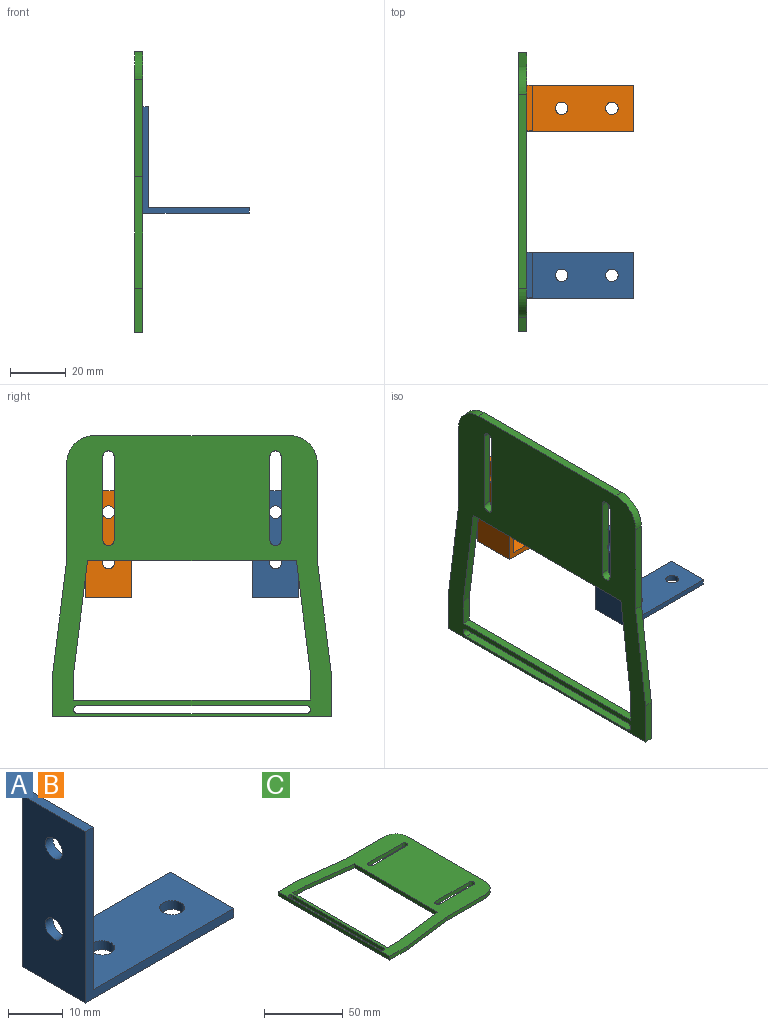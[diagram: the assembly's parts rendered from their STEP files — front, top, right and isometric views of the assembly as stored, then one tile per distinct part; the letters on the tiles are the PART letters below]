
ASSEMBLY  parts=3 mates=2
PART A: 12 faces, bbox 38.3x16.3x38.3 mm
  f0: plane 36.3x16.3mm, normal (0,0,1), area 559.9mm2, adj f1,f3,f4,f5,f6,f11
  f1: plane 38.3x38.3mm, normal (0,1,0), area 149.2mm2, adj f0,f2,f6,f7,f8,f11
  f2: plane 38.3x16.3mm, normal (-1,0,0), area 592.5mm2, adj f1,f3,f7,f8,f9,f10
  f3: plane 38.3x38.3mm, normal (0,-1,0), area 149.2mm2, adj f0,f2,f6,f7,f8,f11
  f4: cylinder r=2.25mm len=4.5mm, axis (0,0,-1), area 28.3mm2, adj f0,f7
  f5: cylinder r=2.25mm len=4.5mm, axis (0,0,-1), area 28.3mm2, adj f0,f7
  f6: plane 16.3x2mm, normal (1,0,0), area 32.6mm2, adj f0,f1,f3,f7
  f7: plane 38.3x16.3mm, normal (0,0,-1), area 592.5mm2, adj f1,f2,f3,f4,f5,f6
  f8: plane 16.3x2mm, normal (0,0,1), area 32.6mm2, adj f1,f2,f3,f11
  f9: cylinder r=2.25mm len=4.5mm, axis (-1,0,0), area 28.3mm2, adj f2,f11
  f10: cylinder r=2.25mm len=4.5mm, axis (-1,0,0), area 28.3mm2, adj f2,f11
  f11: plane 36.3x16.3mm, normal (1,0,0), area 559.9mm2, adj f0,f1,f3,f8,f9,f10
PART B: same geometry as A
PART C: 30 faces, bbox 100.9x100x3 mm
  f0: cylinder r=2mm len=4mm, axis (0,0,-1), area 18.8mm2, adj f1,f27,f28,f29
  f1: plane 30x3mm, normal (0,-1,0), area 90mm2, adj f0,f2,f28,f29
  f2: cylinder r=2mm len=4mm, axis (0,0,-1), area 18.8mm2, adj f1,f27,f28,f29
  f3: plane 85x3mm, normal (1,0,0), area 255mm2, adj f4,f23,f28,f29
  f4: plane 10x3mm, normal (0,-1,0), area 30mm2, adj f3,f5,f28,f29
  f5: plane 40x5mm, normal (-0.12,-0.99,0), area 120.9mm2, adj f4,f6,f28,f29
  f6: plane 75x3mm, normal (-1,0,0), area 225mm2, adj f5,f7,f28,f29
  f7: plane 40x5mm, normal (-0.12,0.99,0), area 120.9mm2, adj f6,f23,f28,f29
  f8: cylinder r=10mm len=10mm, axis (0,0,-1), area 47.1mm2, adj f9,f24,f28,f29
  f9: plane 35x3mm, normal (0,1,0), area 105mm2, adj f8,f10,f28,f29
  f10: plane 40x5mm, normal (0.12,0.99,0), area 120.9mm2, adj f9,f11,f28,f29
  f11: plane 15.9x3mm, normal (0,1,0), area 47.7mm2, adj f10,f12,f28,f29
  f12: plane 100x3mm, normal (-1,0,0), area 300mm2, adj f11,f13,f28,f29
  f13: plane 15.9x3mm, normal (0,-1,0), area 47.7mm2, adj f12,f14,f28,f29
  f14: plane 40x5mm, normal (0.12,-0.99,0), area 120.9mm2, adj f13,f15,f28,f29
  f15: plane 35x3mm, normal (0,-1,0), area 105mm2, adj f14,f16,f28,f29
  f16: cylinder r=10mm len=10mm, axis (0,0,-1), area 47.1mm2, adj f15,f24,f28,f29
  f17: cylinder r=1.5mm len=3mm, axis (0,0,-1), area 14.1mm2, adj f18,f25,f28,f29
  f18: plane 82x3mm, normal (-1,0,0), area 246mm2, adj f17,f19,f28,f29
  f19: cylinder r=1.5mm len=3mm, axis (0,0,-1), area 14.1mm2, adj f18,f25,f28,f29
  f20: plane 30x3mm, normal (0,1,0), area 90mm2, adj f21,f26,f28,f29
  f21: cylinder r=2mm len=4mm, axis (0,0,-1), area 18.8mm2, adj f20,f22,f28,f29
  f22: plane 30x3mm, normal (0,-1,0), area 90mm2, adj f21,f26,f28,f29
  f23: plane 10x3mm, normal (0,1,0), area 30mm2, adj f3,f7,f28,f29
  f24: plane 70x3mm, normal (1,0,0), area 210mm2, adj f8,f16,f28,f29
  f25: plane 82x3mm, normal (1,0,0), area 246mm2, adj f17,f19,f28,f29
  f26: cylinder r=2mm len=4mm, axis (0,0,-1), area 18.8mm2, adj f20,f22,f28,f29
  f27: plane 30x3mm, normal (0,1,0), area 90mm2, adj f0,f2,f28,f29
  f28: plane 100.9x100mm, normal (0,0,1), area 4828.9mm2, adj f0,f1,f2,f3,f4,f5,f6,f7
  f29: plane 100.9x100mm, normal (0,0,-1), area 4828.9mm2, adj f0,f1,f2,f3,f4,f5,f6,f7
PLACE A t=(67.09,-67.47,-11.17)mm
PLACE B rot(axis=(0,1,0),0deg) t=(67.09,-7.47,-11.17)mm
PLACE C rot(axis=(0,-1,0),90deg) t=(16.07,0.96,-31.92)mm
MATE fastened A.f9 <-> C.f29  axis (-1,0,0) through (16.07,-24.04,19.38)mm
MATE fastened B.f9 <-> C.f29  axis (-1,0,0) through (16.07,35.96,19.38)mm
